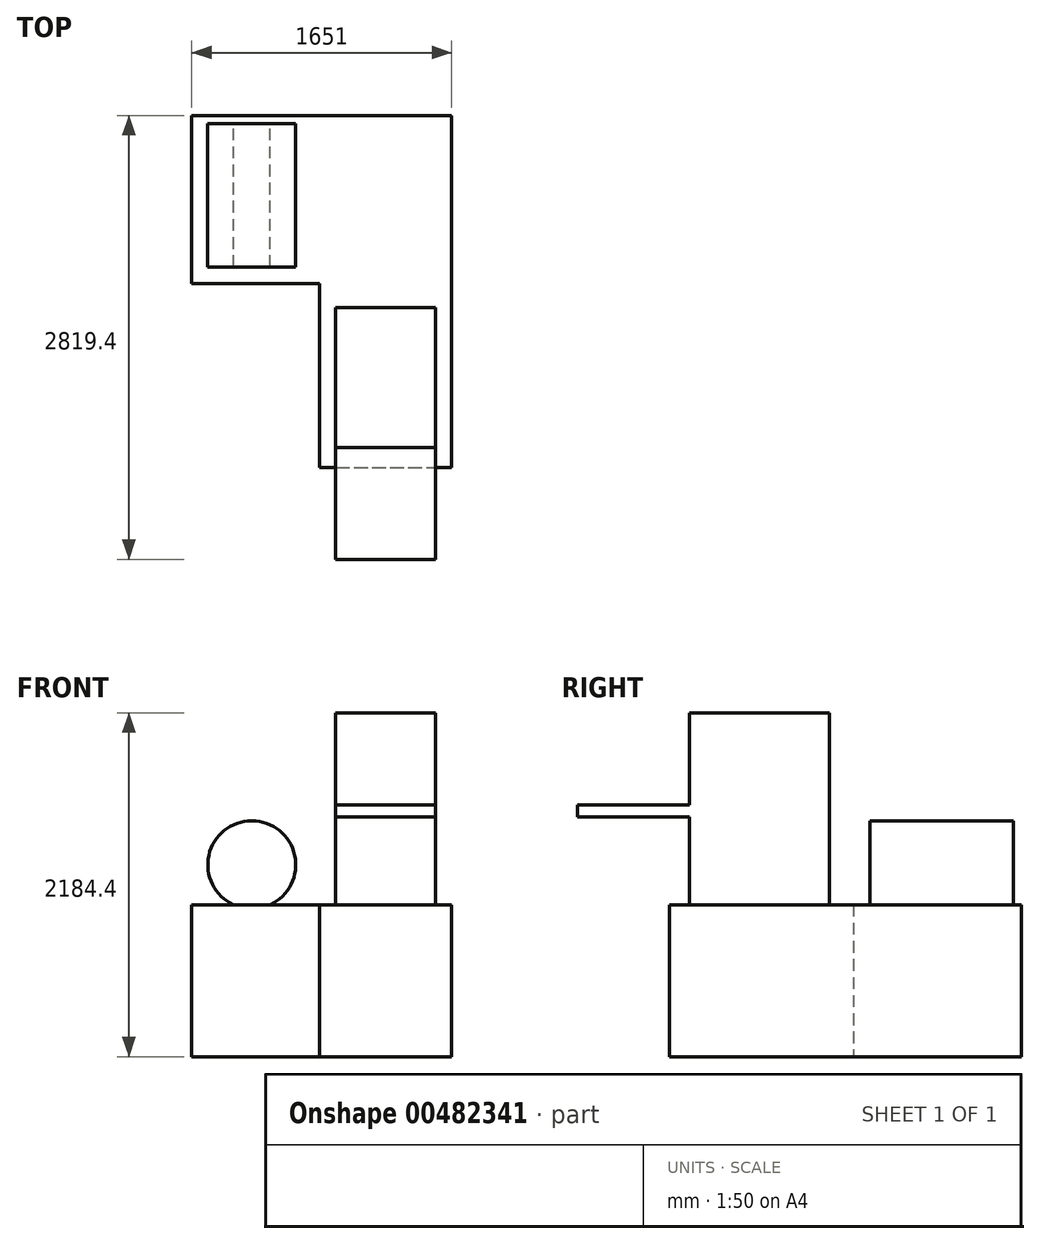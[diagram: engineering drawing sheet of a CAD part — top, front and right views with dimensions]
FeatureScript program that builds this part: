
annotation { "Feature Type Name" : "Feature", "Feature Type Description" : "" }
export const myFeature = defineFeature(function(context is Context, id is Id, definition is map)
    precondition{}
    {
        {
            var Q0;
            Q0=qCreatedBy(makeId("Top.planeOp"),FACE);
            var sketch = newSketch(context, id + "F0", { "sketchPlane" : qUnion([Q0])});
            skLineSegment(sketch, "E0", {"start": v(0, 0) * mm, "end": v(0, -1168.4) * mm});
            skLineSegment(sketch, "E1", {"start": v(0, -1168.4) * mm, "end": v(838.2, -1168.4) * mm});
            skLineSegment(sketch, "E2", {"start": v(838.2, -1168.4) * mm, "end": v(838.2, 1066.8) * mm});
            skLineSegment(sketch, "E3", {"start": v(838.2, 1066.8) * mm, "end": v(-812.8, 1066.8) * mm});
            skLineSegment(sketch, "E4", {"start": v(-812.8, 1066.8) * mm, "end": v(-812.8, 0) * mm});
            skLineSegment(sketch, "E5", {"start": v(-812.8, 0) * mm, "end": v(0, 0) * mm});
            skSolve(sketch);
        }
        {
            var Q0;
            Q0 = qSketchRegion(id + "F0", true);
            extrude(context, id + "F1", {"entities" : qUnion([Q0]), "depth" : 965.2 * mm, "offsetDistance" : 25.4 * mm});
        }
        {
            var Q0;
            Q0=makeQuery(id+"F1.opExtrude","SWEPT_FACE",FACE,{"disambiguationData":[OSD([sQuery(id+"F0.wireOp",EDGE,"E3")])]});
            cPlane(context, id + "F2", {"entities" : qUnion([Q0]), "cplaneType" : CPlaneType.OFFSET, "offset" : 50.8 * mm, "oppositeDirection" : true, "width" : 152.4 * mm, "height" : 152.4 * mm});
        }
        {
            var Q0;
            Q0=qCreatedBy(id+"F2.planeOp",FACE);
            var sketch = newSketch(context, id + "F3", { "sketchPlane" : qUnion([Q0])});
            skCircle(sketch, "E6", {"center": v(431.8, 1219.2) * mm, "radius": 279.4 * mm});
            skSolve(sketch);
        }
        {
            var Q0;
            Q0 = qSketchRegion(id + "F3", true);
            extrude(context, id + "F4", {"entities" : qUnion([Q0]), "operationType" : NewBodyOperationType.ADD, "oppositeDirection" : true, "depth" : 911.86 * mm, "offsetDistance" : 25.4 * mm});
        }
        {
            var Q0;
            Q0=makeQuery(id+"F1.opExtrude","CAP_FACE",FACE,{"disambiguationData":[OSD([sQuery(id+"F0.wireOp",EDGE,"E0"),sQuery(id+"F0.wireOp",EDGE,"E1"),sQuery(id+"F0.wireOp",EDGE,"E2"),sQuery(id+"F0.wireOp",EDGE,"E3"),sQuery(id+"F0.wireOp",EDGE,"E4"),sQuery(id+"F0.wireOp",EDGE,"E5")])],"isStart":false});
            var sketch = newSketch(context, id + "F5", { "sketchPlane" : qUnion([Q0])});
            skLineSegment(sketch, "E7.bottom", {"start": v(101.6, -152.4) * mm, "end": v(736.6, -152.4) * mm});
            skLineSegment(sketch, "E7.top", {"start": v(101.6, -1041.4) * mm, "end": v(736.6, -1041.4) * mm});
            skLineSegment(sketch, "E7.left", {"start": v(101.6, -152.4) * mm, "end": v(101.6, -1041.4) * mm});
            skLineSegment(sketch, "E7.right", {"start": v(736.6, -152.4) * mm, "end": v(736.6, -1041.4) * mm});
            skSolve(sketch);
        }
        {
            var Q0;
            Q0 = qSketchRegion(id + "F5", true);
            extrude(context, id + "F6", {"entities" : qUnion([Q0]), "operationType" : NewBodyOperationType.ADD, "depth" : 1219.2 * mm, "offsetDistance" : 25.4 * mm});
        }
        {
            var Q0;
            Q0=makeQuery(id+"F6.opExtrude","SWEPT_FACE",FACE,{"disambiguationData":[OSD([sQuery(id+"F5.wireOp",EDGE,"E7.left")])]});
            var sketch = newSketch(context, id + "F7", { "sketchPlane" : qUnion([Q0])});
            skLineSegment(sketch, "E8.bottom", {"start": v(1041.4, 1600.2) * mm, "end": v(1752.6, 1600.2) * mm});
            skLineSegment(sketch, "E8.top", {"start": v(1041.4, 1524) * mm, "end": v(1752.6, 1524) * mm});
            skLineSegment(sketch, "E8.left", {"start": v(1041.4, 1600.2) * mm, "end": v(1041.4, 1524) * mm});
            skLineSegment(sketch, "E8.right", {"start": v(1752.6, 1600.2) * mm, "end": v(1752.6, 1524) * mm});
            skSolve(sketch);
        }
        {
            var Q0;
            Q0 = qSketchRegion(id + "F7", true);
            var Q1;
            Q1=makeQuery(id+"F6.opExtrude","SWEPT_FACE",FACE,{"disambiguationData":[OSD([sQuery(id+"F5.wireOp",EDGE,"E7.right")])]});
            extrude(context, id + "F8", {"entities" : qUnion([Q0]), "operationType" : NewBodyOperationType.ADD, "endBound" : BoundingType.UP_TO_SURFACE, "oppositeDirection" : true, "depth" : 25.4 * mm, "endBoundEntityFace" : qUnion([Q1]), "offsetDistance" : 25.4 * mm});
        }
    });
